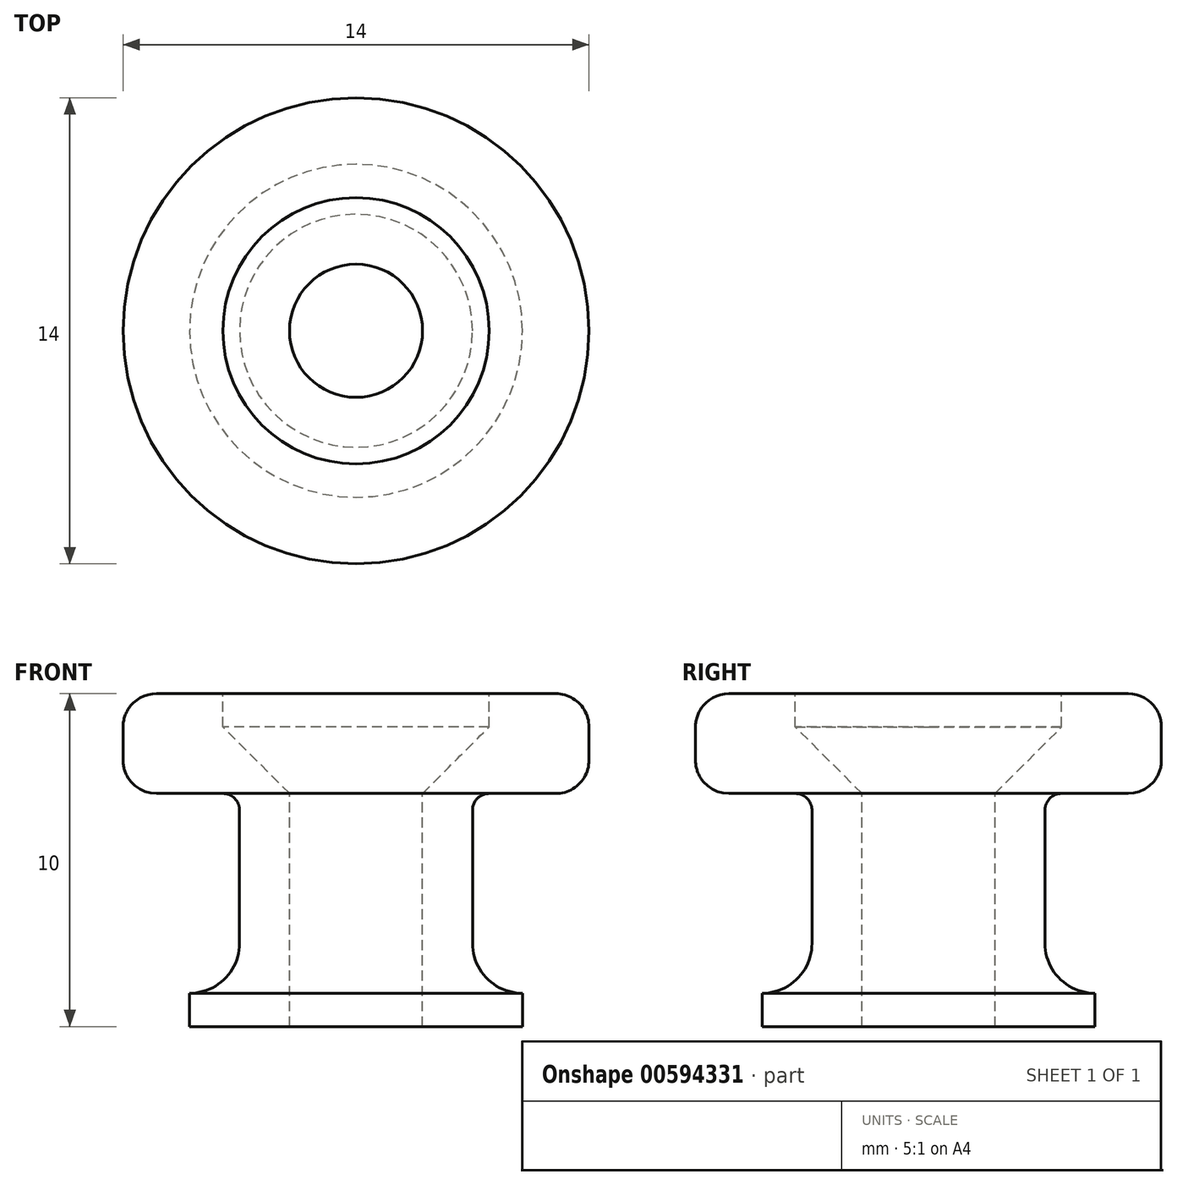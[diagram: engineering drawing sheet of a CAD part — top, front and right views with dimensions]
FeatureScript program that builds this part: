
annotation { "Feature Type Name" : "Feature", "Feature Type Description" : "" }
export const myFeature = defineFeature(function(context is Context, id is Id, definition is map)
    precondition{}
    {
        {
            var Q0;
            Q0=qCreatedBy(makeId("Front.planeOp"),FACE);
            var sketch = newSketch(context, id + "F0", { "sketchPlane" : qUnion([Q0])});
            skLineSegment(sketch, "E0", {"start": v(0, 6.88) * mm, "end": v(0, -7.35) * mm, "construction": true});
            skLineSegment(sketch, "E1", {"start": v(-2, 0) * mm, "end": v(-2, 7) * mm});
            skLineSegment(sketch, "E2", {"start": v(-2, 7) * mm, "end": v(-4, 9) * mm});
            skLineSegment(sketch, "E3", {"start": v(-4, 9) * mm, "end": v(-4, 10) * mm});
            skLineSegment(sketch, "E4", {"start": v(-4, 10) * mm, "end": v(-6, 10) * mm});
            skLineSegment(sketch, "E5", {"start": v(-7, 9) * mm, "end": v(-7, 8) * mm});
            skLineSegment(sketch, "E6", {"start": v(-6, 7) * mm, "end": v(-4, 7) * mm});
            skLineSegment(sketch, "E7", {"start": v(-3.5, 6.5) * mm, "end": v(-3.5, 2.5) * mm});
            skLineSegment(sketch, "E8", {"start": v(-5, 1) * mm, "end": v(-5, 1) * mm});
            skLineSegment(sketch, "E9", {"start": v(-5, 1) * mm, "end": v(-5, 0) * mm});
            skLineSegment(sketch, "E10", {"start": v(-5, 0) * mm, "end": v(-2, 0) * mm});
            skPoint(sketch, "E11.visualSharp", {"position": v(-7, 10) * mm});
            skArc(sketch, "E11.filletArc", {"start": v(-6, 10) * mm, "mid": v(-6.7, 9.7) * mm, "end": v(-7, 9) * mm});
            skPoint(sketch, "E12.visualSharp", {"position": v(-7, 7) * mm});
            skArc(sketch, "E12.filletArc", {"start": v(-7, 8) * mm, "mid": v(-6.7, 7.3) * mm, "end": v(-6, 7) * mm});
            skPoint(sketch, "E13.visualSharp", {"position": v(-3.5, 7) * mm});
            skArc(sketch, "E13.filletArc", {"start": v(-3.5, 6.5) * mm, "mid": v(-3.65, 6.85) * mm, "end": v(-4, 7) * mm});
            skPoint(sketch, "E14.visualSharp", {"position": v(-3.5, 1) * mm});
            skArc(sketch, "E14.filletArc", {"start": v(-5, 1) * mm, "mid": v(-3.94, 1.44) * mm, "end": v(-3.5, 2.5) * mm});
            skSolve(sketch);
        }
        {
            var Q0;
            Q0 = qSketchRegion(id + "F0", true);
            var Q1;
            Q1=sQuery(id+"F0.wireOp",EDGE,"E0");
            revolve(context, id + "F1", {"entities" : qUnion([Q0]), "axis" : qUnion([Q1]), "revolveType" : RevolveType.FULL});
        }
    });
